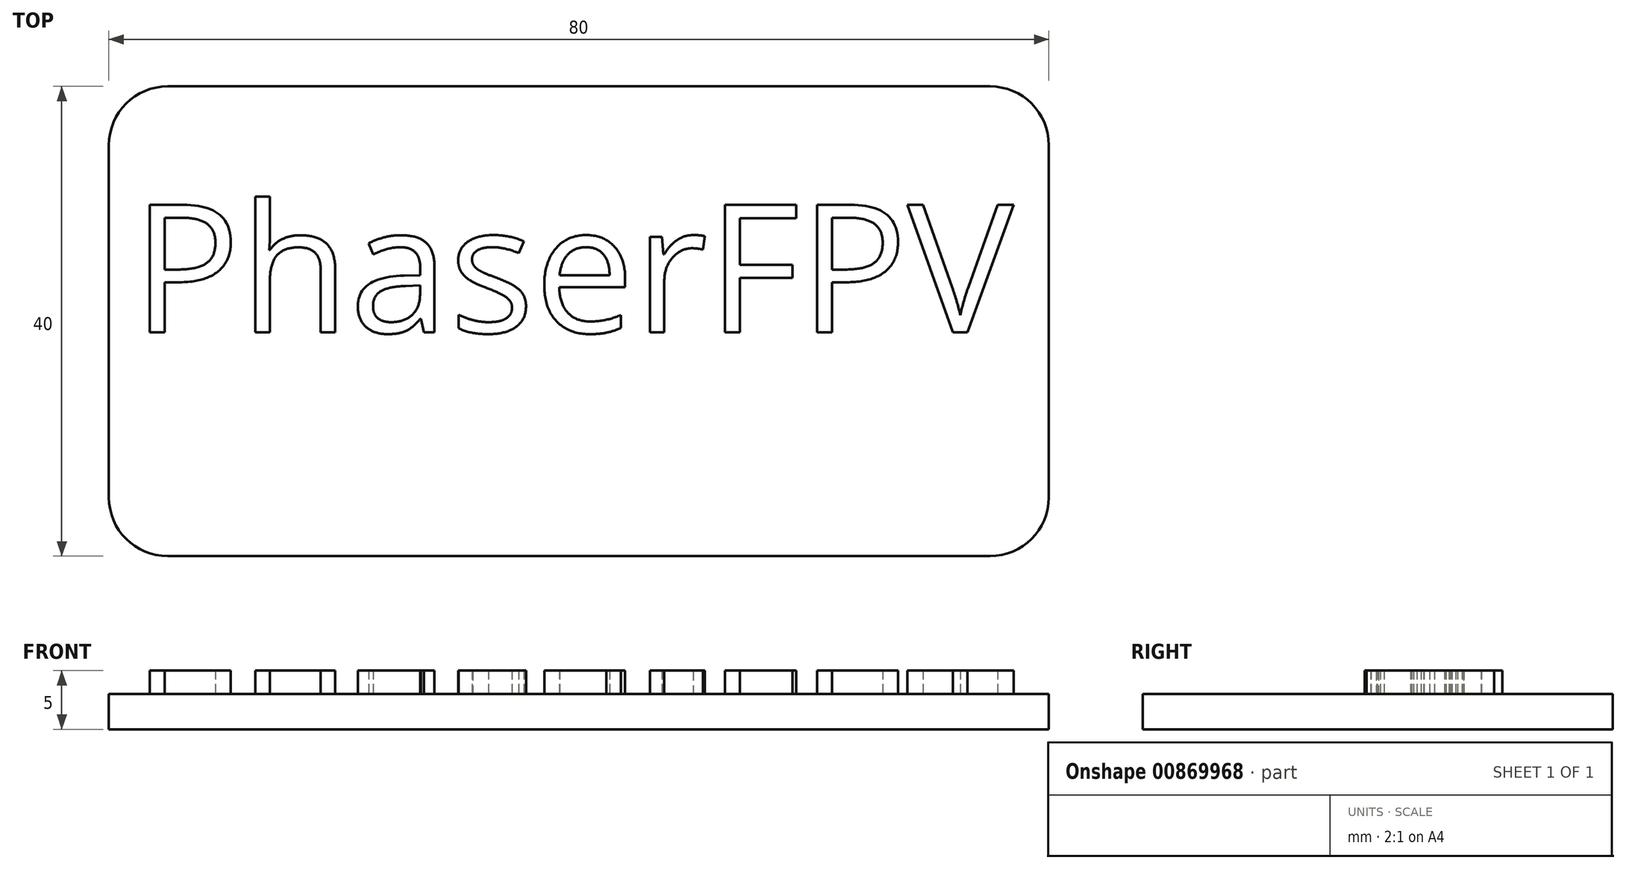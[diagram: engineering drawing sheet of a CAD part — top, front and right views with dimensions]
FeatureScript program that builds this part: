
annotation { "Feature Type Name" : "Feature", "Feature Type Description" : "" }
export const myFeature = defineFeature(function(context is Context, id is Id, definition is map)
    precondition{}
    {
        {
            var Q0;
            Q0=qCreatedBy(makeId("Top.planeOp"),FACE);
            var sketch = newSketch(context, id + "F0", { "sketchPlane" : qUnion([Q0])});
            skLineSegment(sketch, "E0.bottom", {"start": v(-39.82, 37.57) * mm, "end": v(40.18, 37.57) * mm});
            skLineSegment(sketch, "E0.top", {"start": v(-39.82, -2.43) * mm, "end": v(40.18, -2.43) * mm});
            skLineSegment(sketch, "E0.left", {"start": v(-39.82, 37.57) * mm, "end": v(-39.82, -2.43) * mm});
            skLineSegment(sketch, "E0.right", {"start": v(40.18, 37.57) * mm, "end": v(40.18, -2.43) * mm});
            skSolve(sketch);
        }
        {
            var Q0;
            Q0 = qSketchRegion(id + "F0", true);
            extrude(context, id + "F1", {"entities" : qUnion([Q0]), "depth" : 3 * mm, "offsetDistance" : 25 * mm});
        }
        {
            var Q0;
            Q0=makeQuery(id+"F1.opExtrude","CAP_FACE",FACE,{"disambiguationData":[OSD([sQuery(id+"F0.wireOp",EDGE,"E0.bottom"),sQuery(id+"F0.wireOp",EDGE,"E0.top"),sQuery(id+"F0.wireOp",EDGE,"E0.left"),sQuery(id+"F0.wireOp",EDGE,"E0.right")])],"isStart":false});
            var sketch = newSketch(context, id + "F2", { "sketchPlane" : qUnion([Q0])});
            skText(sketch, "E1", { "text": "PhaserFPV", "fontName": "OpenSans-Regular.ttf"});
            const initialGuessF2  = {"E1": [-0.03782, 0.01662, 1, 0, 0.01095]};
            skSetInitialGuess(sketch, initialGuessF2);
            skSolve(sketch);
        }
        {
            var Q0;
            Q0 = qSketchRegion(id + "F2", true);
            extrude(context, id + "F3", {"entities" : qUnion([Q0]), "operationType" : NewBodyOperationType.ADD, "depth" : 2 * mm, "offsetDistance" : 25 * mm});
        }
        {
            var Q0;
            Q0=makeQuery(id+"F1.opExtrude","SWEPT_EDGE",EDGE,{"disambiguationData":[OSD([sQuery(id+"F0.wireOp",EDGE,"E0.top"),sQuery(id+"F0.wireOp",EDGE,"E0.left")])]});
            var Q1;
            Q1=makeQuery(id+"F1.opExtrude","SWEPT_EDGE",EDGE,{"disambiguationData":[OSD([sQuery(id+"F0.wireOp",EDGE,"E0.top"),sQuery(id+"F0.wireOp",EDGE,"E0.right")])]});
            var Q2;
            Q2=makeQuery(id+"F1.opExtrude","SWEPT_EDGE",EDGE,{"disambiguationData":[OSD([sQuery(id+"F0.wireOp",EDGE,"E0.bottom"),sQuery(id+"F0.wireOp",EDGE,"E0.right")])]});
            var Q3;
            Q3=makeQuery(id+"F1.opExtrude","SWEPT_EDGE",EDGE,{"disambiguationData":[OSD([sQuery(id+"F0.wireOp",EDGE,"E0.bottom"),sQuery(id+"F0.wireOp",EDGE,"E0.left")])]});
            fillet(context, id + "F4", {"entities" : qUnion([Q0, Q1, Q2, Q3]), "radius" : 5 * mm, "tangentPropagation" : true, "allowEdgeOverflow" : false});
        }
    });
